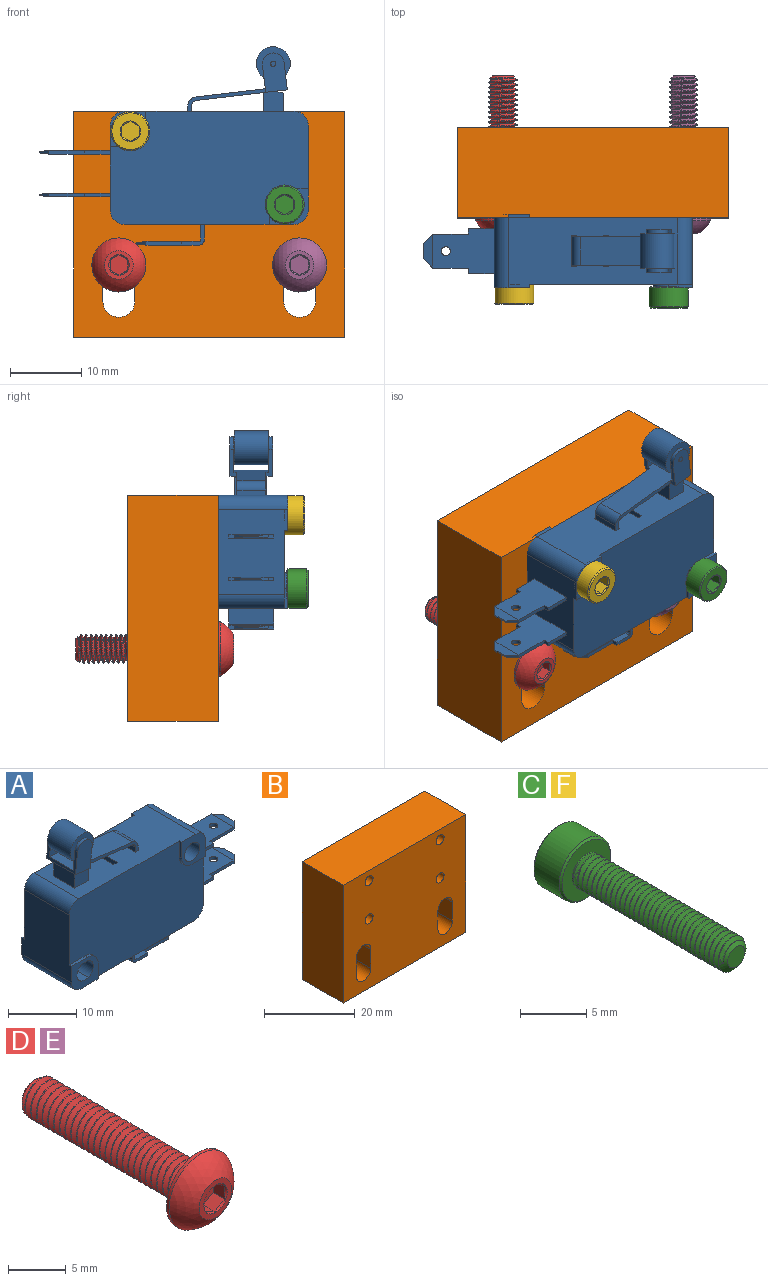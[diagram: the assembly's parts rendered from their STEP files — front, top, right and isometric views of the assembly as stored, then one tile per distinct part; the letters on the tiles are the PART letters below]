
ASSEMBLY  parts=6 mates=5
PART A: 124 faces, bbox 37.8x10.3x27.9 mm
  f0: cylinder r=0.64mm len=1.27mm, axis (0,0,1), area 2mm2, adj f84,f85
  f1: cylinder r=0.64mm len=1.27mm, axis (0,0,1), area 2mm2, adj f73,f74
  f2: cylinder r=0.64mm len=1.27mm, axis (0,0,1), area 2mm2, adj f51,f53
  f3: cylinder r=1.7mm len=10.31mm, axis (0,1,0), area 40.2mm2, adj f6,f11,f13,f15
  f4: cylinder r=1.55mm len=10.31mm, axis (0,1,0), area 100.4mm2, adj f5,f12
  f5: plane 5x5mm, normal (0,1,0), area 15.6mm2, adj f4,f9,f10,f19,f42,f43,f44
  f6: plane 5.5x5mm, normal (0,1,0), area 16.8mm2, adj f3,f7,f8,f13,f14,f15,f16,f45
  f7: plane 11.9x10.31mm, normal (-1,0,0), area 113.8mm2, adj f6,f11,f16,f18,f37,f41,f45,f48
  f8: plane 23.8x10.31mm, normal (0,0,-1), area 221.9mm2, adj f6,f11,f16,f17,f35,f41,f47,f48
  f9: plane 11.9x10.31mm, normal (1,0,0), area 107.3mm2, adj f5,f12,f17,f19,f40,f41,f42,f48
  f10: plane 23.8x10.31mm, normal (0,0,1), area 205.5mm2, adj f5,f12,f18,f19,f20,f21,f22,f23
  f11: plane 5.5x5mm, normal (0,-1,0), area 16.8mm2, adj f3,f7,f8,f13,f14,f15,f16,f35
  f12: plane 5x5mm, normal (0,-1,0), area 15.6mm2, adj f4,f9,f10,f19,f38,f39,f40
  f13: plane 10.31x1.4mm, normal (0,0,1), area 14.4mm2, adj f3,f6,f11,f14
  f14: cylinder r=1.7mm len=10.31mm, axis (0,1,0), area 40.2mm2, adj f6,f11,f13,f15
  f15: plane 10.31x1.4mm, normal (0,0,-1), area 14.4mm2, adj f3,f6,f11,f14
  f16: cylinder r=2mm len=10.31mm, axis (0,1,0), area 32.4mm2, adj f6,f7,f8,f11
  f17: cylinder r=2mm len=9.31mm, axis (0,1,0), area 29.2mm2, adj f8,f9,f41,f48
  f18: cylinder r=2mm len=9.31mm, axis (0,1,0), area 29.2mm2, adj f7,f10,f41,f48
  f19: cylinder r=2mm len=10.31mm, axis (0,1,0), area 32.4mm2, adj f5,f9,f10,f12
  f20: plane 2.85x2mm, normal (0,1,0), area 4.4mm2, adj f10,f21,f23,f24,f115,f116,f117
  f21: plane 4.25x2mm, normal (1,0,0), area 8.5mm2, adj f10,f20,f22,f24
  f22: plane 2.85x2mm, normal (0,-1,0), area 5.7mm2, adj f10,f21,f23,f24
  f23: plane 4.25x2mm, normal (-1,0,0), area 8.5mm2, adj f10,f20,f22,f24
  f24: plane 4.25x2.85mm, normal (0,0,1), area 12.1mm2, adj f20,f21,f22,f23
  f25: plane 4.25x2mm, normal (1,0,0), area 8.5mm2, adj f10,f26,f28,f29
  f26: plane 2x0.76mm, normal (0,-1,0), area 1.5mm2, adj f10,f25,f27,f29
  f27: plane 4.25x2mm, normal (-1,0,0), area 8.5mm2, adj f10,f26,f28,f29
  f28: plane 2x0.76mm, normal (0,1,0), area 1.5mm2, adj f10,f25,f27,f29
  f29: plane 4.25x0.76mm, normal (0,0,1), area 3.2mm2, adj f25,f26,f27,f28
  f30: plane 4.25x2mm, normal (1,0,0), area 8.5mm2, adj f10,f31,f33,f34
  f31: plane 2x0.76mm, normal (0,-1,0), area 1.5mm2, adj f10,f30,f32,f34
  f32: plane 4.25x2mm, normal (-1,0,0), area 8.5mm2, adj f10,f31,f33,f34
  f33: plane 2x0.76mm, normal (0,1,0), area 1.5mm2, adj f10,f30,f32,f34
  f34: plane 4.25x0.76mm, normal (0,0,1), area 3.2mm2, adj f30,f31,f32,f33
  f35: plane 2.8x0.5mm, normal (1,0,0), area 1.4mm2, adj f8,f11,f36,f41
  f36: cylinder r=2.2mm len=2.2mm, axis (0,-1,0), area 1.7mm2, adj f11,f35,f37,f41
  f37: plane 3.3x0.5mm, normal (0,0,1), area 1.6mm2, adj f7,f11,f36,f41
  f38: plane 2.8x0.5mm, normal (-1,0,0), area 1.4mm2, adj f10,f12,f39,f41
  f39: cylinder r=2.2mm len=2.2mm, axis (0,-1,0), area 1.7mm2, adj f12,f38,f40,f41
  f40: plane 2.8x0.5mm, normal (0,0,-1), area 1.4mm2, adj f9,f12,f39,f41
  f41: plane 27.8x15.9mm, normal (0,-1,0), area 389.9mm2, adj f7,f8,f9,f10,f17,f18,f35,f36
  f42: plane 2.8x0.5mm, normal (0,0,-1), area 1.4mm2, adj f5,f9,f43,f48
  f43: cylinder r=2.2mm len=2.2mm, axis (0,1,0), area 1.7mm2, adj f5,f42,f44,f48
  f44: plane 2.8x0.5mm, normal (-1,0,0), area 1.4mm2, adj f5,f10,f43,f48
  f45: plane 3.3x0.5mm, normal (0,0,1), area 1.6mm2, adj f6,f7,f46,f48
  f46: cylinder r=2.2mm len=2.2mm, axis (0,1,0), area 1.7mm2, adj f6,f45,f47,f48
  f47: plane 2.8x0.5mm, normal (1,0,0), area 1.4mm2, adj f6,f8,f46,f48
  f48: plane 27.8x15.9mm, normal (0,1,0), area 389.9mm2, adj f7,f8,f9,f10,f17,f18,f42,f43
  f49: plane 6.35x2.19mm, normal (-1,0,0), area 13.9mm2, adj f8,f50,f56,f57
  f50: cylinder r=0.71mm len=6.35mm, axis (0,1,0), area 7.1mm2, adj f49,f51,f56,f57
  f51: plane 7.48x6.35mm, normal (0,0,-1), area 38.1mm2, adj f2,f50,f56,f57,f59,f60,f61,f63
  f52: plane 2.12x0.17mm, normal (1,0,0), area 0.4mm2, adj f58,f62,f86,f87
  f53: plane 7.48x6.35mm, normal (0,0,1), area 38.1mm2, adj f2,f54,f56,f57,f59,f60,f61,f63
  f54: cylinder r=0.2mm len=6.35mm, axis (0,1,0), area 2mm2, adj f53,f55,f56,f57
  f55: plane 6.35x2.19mm, normal (1,0,0), area 13.9mm2, adj f8,f54,f56,f57
  f56: plane 3.15x2.9mm, normal (0,-1,0), area 2.7mm2, adj f8,f49,f50,f51,f53,f54,f55,f63
  f57: plane 3.15x2.9mm, normal (0,1,0), area 2.7mm2, adj f8,f49,f50,f51,f53,f54,f55,f60
  f58: plane 1.32x1.32mm, normal (0.71,0.71,0), area 0.6mm2, adj f52,f59,f86,f87
  f59: plane 5.03x0.51mm, normal (0,1,0), area 2.6mm2, adj f51,f53,f58,f60
  f60: plane 0.8x0.51mm, normal (1,0,0), area 0.4mm2, adj f51,f53,f57,f59
  f61: plane 5.03x0.51mm, normal (0,-1,0), area 2.6mm2, adj f51,f53,f62,f63
  f62: plane 1.32x1.32mm, normal (0.71,-0.71,0), area 0.6mm2, adj f52,f61,f86,f87
  f63: plane 0.8x0.51mm, normal (1,0,0), area 0.4mm2, adj f51,f53,f56,f61
  f64: plane 3.65x0.51mm, normal (0,1,0), area 1.9mm2, adj f9,f65,f73,f74
  f65: plane 0.8x0.51mm, normal (1,0,0), area 0.4mm2, adj f64,f66,f73,f74
  f66: plane 5.03x0.51mm, normal (0,1,0), area 2.6mm2, adj f65,f67,f73,f74
  f67: plane 1.32x1.32mm, normal (0.71,0.71,0), area 0.6mm2, adj f66,f68,f88,f89
  f68: plane 2.12x0.17mm, normal (1,0,0), area 0.4mm2, adj f67,f69,f88,f89
  f69: plane 1.32x1.32mm, normal (0.71,-0.71,0), area 0.6mm2, adj f68,f70,f88,f89
  f70: plane 5.03x0.51mm, normal (0,-1,0), area 2.6mm2, adj f69,f71,f73,f74
  f71: plane 0.8x0.51mm, normal (1,0,0), area 0.4mm2, adj f70,f72,f73,f74
  f72: plane 3.65x0.51mm, normal (0,-1,0), area 1.9mm2, adj f9,f71,f73,f74
  f73: plane 8.68x6.35mm, normal (0,0,-1), area 45.8mm2, adj f1,f9,f64,f65,f66,f70,f71,f72
  f74: plane 8.68x6.35mm, normal (0,0,1), area 45.8mm2, adj f1,f9,f64,f65,f66,f70,f71,f72
  f75: plane 3.65x0.51mm, normal (0,1,0), area 1.9mm2, adj f9,f76,f84,f85
  f76: plane 0.8x0.51mm, normal (1,0,0), area 0.4mm2, adj f75,f77,f84,f85
  f77: plane 5.03x0.51mm, normal (0,1,0), area 2.6mm2, adj f76,f78,f84,f85
  f78: plane 1.32x1.32mm, normal (0.71,0.71,0), area 0.6mm2, adj f77,f79,f90,f91
  f79: plane 2.12x0.17mm, normal (1,0,0), area 0.4mm2, adj f78,f80,f90,f91
  f80: plane 1.32x1.32mm, normal (0.71,-0.71,0), area 0.6mm2, adj f79,f81,f90,f91
  f81: plane 5.03x0.51mm, normal (0,-1,0), area 2.6mm2, adj f80,f82,f84,f85
  f82: plane 0.8x0.51mm, normal (1,0,0), area 0.4mm2, adj f81,f83,f84,f85
  f83: plane 3.65x0.51mm, normal (0,-1,0), area 1.9mm2, adj f9,f82,f84,f85
  f84: plane 8.68x6.35mm, normal (0,0,-1), area 45.8mm2, adj f0,f9,f75,f76,f77,f81,f82,f83
  f85: plane 8.68x6.35mm, normal (0,0,1), area 45.8mm2, adj f0,f9,f75,f76,f77,f81,f82,f83
  f86: plane 4.75x1.32mm, normal (0.13,0,0.99), area 4.6mm2, adj f52,f53,f58,f62
  f87: plane 4.75x1.32mm, normal (0.13,0,-0.99), area 4.6mm2, adj f51,f52,f58,f62
  f88: plane 4.75x1.32mm, normal (0.13,0,0.99), area 4.6mm2, adj f67,f68,f69,f74
  f89: plane 4.75x1.32mm, normal (0.13,0,-0.99), area 4.6mm2, adj f67,f68,f69,f73
  f90: plane 4.75x1.32mm, normal (0.13,0,0.99), area 4.6mm2, adj f78,f79,f80,f85
  f91: plane 4.75x1.32mm, normal (0.13,0,-0.99), area 4.6mm2, adj f78,f79,f80,f84
  f92: plane 2.8x2.8mm, normal (0,-1,0), area 7.6mm2, adj f10,f93,f112,f113,f116,f117
  f93: plane 12.76x6mm, normal (-0.12,0,-0.99), area 53.8mm2, adj f92,f100,f101,f103,f104,f106,f108,f110
  f94: cylinder r=0.38mm len=0.76mm, axis (0,1,0), area 1.3mm2, adj f104,f107
  f95: cylinder r=1.52mm len=3.04mm, axis (0,-1,0), area 2.7mm2, adj f100,f103,f105,f106
  f96: plane 12.76x4.88mm, normal (0.12,0,0.99), area 54.7mm2, adj f99,f100,f105,f106,f107,f108,f110,f111
  f97: plane 4.06x0.51mm, normal (0,0,-1), area 2.1mm2, adj f98,f102,f110,f111
  f98: plane 4.06x1.21mm, normal (1,0,0), area 4.9mm2, adj f97,f99,f110,f111
  f99: cylinder r=1.3mm len=4.06mm, axis (0,1,0), area 7.7mm2, adj f96,f98,f110,f111
  f100: plane 6x3.83mm, normal (-0.99,0,0.12), area 6.8mm2, adj f93,f95,f96,f103,f104,f105,f107,f109
  f101: cylinder r=0.79mm len=4.06mm, axis (0,1,0), area 4.7mm2, adj f93,f102,f110,f111
  f102: plane 4.06x1.21mm, normal (-1,0,0), area 4.9mm2, adj f97,f101,f110,f111
  f103: plane 5.53x3.49mm, normal (0,-1,0), area 15.4mm2, adj f93,f95,f100,f106
  f104: plane 5.53x3.49mm, normal (0,1,0), area 15mm2, adj f93,f94,f100,f108,f109
  f105: plane 5.03x3.43mm, normal (0,1,0), area 12.9mm2, adj f95,f96,f100,f106,f123
  f106: plane 3.83x0.97mm, normal (0.99,0,-0.12), area 2.4mm2, adj f93,f95,f96,f103,f105,f111
  f107: plane 5.03x3.43mm, normal (0,-1,0), area 13.4mm2, adj f94,f96,f100,f108,f109
  f108: plane 3.83x0.97mm, normal (0.99,0,-0.12), area 2.4mm2, adj f93,f96,f104,f107,f109,f110
  f109: cylinder r=1.52mm len=3.04mm, axis (0,1,0), area 2.7mm2, adj f100,f104,f107,f108
  f110: plane 10.94x3.65mm, normal (0,1,0), area 6.4mm2, adj f93,f96,f97,f98,f99,f101,f102,f108
  f111: plane 10.94x3.65mm, normal (0,-1,0), area 6.4mm2, adj f93,f96,f97,f98,f99,f101,f102,f106
  f112: cylinder r=4mm len=4.4mm, axis (0,1,0), area 2.1mm2, adj f92,f93,f114,f116
  f113: cylinder r=4mm len=4.4mm, axis (0,1,0), area 6.2mm2, adj f92,f93,f114,f117
  f114: plane 3.25x2.8mm, normal (0,1,0), area 8.9mm2, adj f93,f112,f113,f115,f116,f117
  f115: plane 4.23x2.8mm, normal (0,0,-1), area 11.8mm2, adj f20,f114,f116,f117
  f116: plane 4.4x3mm, normal (1,0,0), area 13.1mm2, adj f10,f20,f92,f112,f114,f115
  f117: plane 4.4x3mm, normal (-1,0,0), area 13.1mm2, adj f10,f20,f92,f113,f114,f115
  f118: plane 0.71x0.71mm, normal (0,1,0), area 0.4mm2, adj f122
  f119: plane 4.8x4.8mm, normal (0,1,0), area 17.7mm2, adj f121,f122
  f120: plane 4.8x4.8mm, normal (0,-1,0), area 17.1mm2, adj f121,f123
  f121: cylinder r=2.4mm len=4.8mm, axis (0,1,0), area 72.4mm2, adj f119,f120
  f122: cylinder r=0.36mm len=0.71mm, axis (0,-1,0), area 1.3mm2, adj f118,f119
  f123: cylinder r=0.56mm len=1.12mm, axis (0,-1,0), area 0.1mm2, adj f105,f120
PART B: 18 faces, bbox 38.1x12.7x31.8 mm
  f0: plane 38.1x31.75mm, normal (0,-1,0), area 1112.5mm2, adj f2,f3,f4,f5,f6,f7,f8,f9
  f1: plane 38.1x31.75mm, normal (0,1,0), area 1112.5mm2, adj f2,f3,f4,f5,f6,f7,f8,f9
  f2: plane 31.75x12.7mm, normal (1,0,0), area 403.2mm2, adj f0,f1,f3,f5
  f3: plane 38.1x12.7mm, normal (0,0,1), area 483.9mm2, adj f0,f1,f2,f4
  f4: plane 31.75x12.7mm, normal (-1,0,0), area 403.2mm2, adj f0,f1,f3,f5
  f5: plane 38.1x12.7mm, normal (0,0,-1), area 483.9mm2, adj f0,f1,f2,f4
  f6: cylinder r=1.25mm len=12.7mm, axis (0,-1,0), area 99.7mm2, adj f0,f1
  f7: cylinder r=1.25mm len=12.7mm, axis (0,-1,0), area 99.7mm2, adj f0,f1
  f8: cylinder r=1.25mm len=12.7mm, axis (0,-1,0), area 99.7mm2, adj f0,f1
  f9: cylinder r=1.25mm len=12.7mm, axis (0,-1,0), area 99.7mm2, adj f0,f1
  f10: cylinder r=2.25mm len=12.7mm, axis (0,-1,0), area 89.8mm2, adj f0,f1,f11,f13
  f11: plane 12.7x5.08mm, normal (-1,0,0), area 64.5mm2, adj f0,f1,f10,f12
  f12: cylinder r=2.25mm len=12.7mm, axis (0,-1,0), area 89.8mm2, adj f0,f1,f11,f13
  f13: plane 12.7x5.08mm, normal (1,0,0), area 64.5mm2, adj f0,f1,f10,f12
  f14: cylinder r=2.25mm len=12.7mm, axis (0,-1,0), area 89.8mm2, adj f0,f1,f15,f17
  f15: plane 12.7x5.08mm, normal (-1,0,0), area 64.5mm2, adj f0,f1,f14,f16
  f16: cylinder r=2.25mm len=12.7mm, axis (0,-1,0), area 89.8mm2, adj f0,f1,f15,f17
  f17: plane 12.7x5.08mm, normal (1,0,0), area 64.5mm2, adj f0,f1,f14,f16
PART C: 57 faces, bbox 6x19.6x6 mm
  f0: cylinder r=1.5mm len=3mm, axis (0,-1,0), area 0.3mm2, adj f1,f32,f33,f35,f36
  f1: cylinder r=1.5mm len=3mm, axis (0,-1,0), area 0.6mm2, adj f0,f2,f32,f33
  f2: cylinder r=1.5mm len=3mm, axis (0,-1,0), area 0.6mm2, adj f1,f3,f32,f33
  f3: cylinder r=1.5mm len=3mm, axis (0,-1,0), area 0.6mm2, adj f2,f4,f32,f33
  f4: cylinder r=1.5mm len=3mm, axis (0,-1,0), area 0.6mm2, adj f3,f5,f32,f33
  f5: cylinder r=1.5mm len=3mm, axis (0,-1,0), area 0.6mm2, adj f4,f6,f32,f33
  f6: cylinder r=1.5mm len=3mm, axis (0,-1,0), area 0.6mm2, adj f5,f7,f32,f33
  f7: cylinder r=1.5mm len=3mm, axis (0,-1,0), area 0.6mm2, adj f6,f8,f32,f33
  f8: cylinder r=1.5mm len=3mm, axis (0,-1,0), area 0.6mm2, adj f7,f9,f32,f33
  f9: cylinder r=1.5mm len=3mm, axis (0,-1,0), area 0.6mm2, adj f8,f10,f32,f33
  f10: cylinder r=1.5mm len=3mm, axis (0,-1,0), area 0.6mm2, adj f9,f11,f32,f33
  f11: cylinder r=1.5mm len=3mm, axis (0,-1,0), area 0.6mm2, adj f10,f12,f32,f33
  f12: cylinder r=1.5mm len=3mm, axis (0,-1,0), area 0.6mm2, adj f11,f13,f32,f33
  f13: cylinder r=1.5mm len=3mm, axis (0,-1,0), area 0.6mm2, adj f12,f14,f32,f33
  f14: cylinder r=1.5mm len=3mm, axis (0,-1,0), area 0.6mm2, adj f13,f15,f32,f33
  f15: cylinder r=1.5mm len=3mm, axis (0,-1,0), area 0.6mm2, adj f14,f16,f32,f33
  f16: cylinder r=1.5mm len=3mm, axis (0,-1,0), area 0.6mm2, adj f15,f17,f32,f33
  f17: cylinder r=1.5mm len=3mm, axis (0,-1,0), area 0.6mm2, adj f16,f18,f32,f33
  f18: cylinder r=1.5mm len=3mm, axis (0,-1,0), area 0.6mm2, adj f17,f19,f32,f33
  f19: cylinder r=1.5mm len=3mm, axis (0,-1,0), area 0.6mm2, adj f18,f20,f32,f33
  f20: cylinder r=1.5mm len=3mm, axis (0,-1,0), area 0.6mm2, adj f19,f21,f32,f33
  f21: cylinder r=1.5mm len=3mm, axis (0,-1,0), area 0.6mm2, adj f20,f22,f32,f33
  f22: cylinder r=1.5mm len=3mm, axis (0,-1,0), area 0.6mm2, adj f21,f23,f32,f33
  f23: cylinder r=1.5mm len=3mm, axis (0,-1,0), area 0.6mm2, adj f22,f24,f32,f33
  f24: cylinder r=1.5mm len=3mm, axis (0,-1,0), area 0.6mm2, adj f23,f25,f32,f33
  f25: cylinder r=1.5mm len=3mm, axis (0,-1,0), area 0.6mm2, adj f24,f26,f32,f33
  f26: cylinder r=1.5mm len=3mm, axis (0,-1,0), area 0.6mm2, adj f25,f27,f32,f33
  f27: cylinder r=1.5mm len=3mm, axis (0,-1,0), area 0.6mm2, adj f26,f28,f32,f33
  f28: cylinder r=1.5mm len=3mm, axis (0,-1,0), area 0.6mm2, adj f27,f29,f32,f33
  f29: cylinder r=1.5mm len=3mm, axis (0,-1,0), area 0.6mm2, adj f28,f30,f32,f33
  f30: cylinder r=1.5mm len=3mm, axis (0,-1,0), area 0.6mm2, adj f29,f31,f32,f33
  f31: cylinder r=1.5mm len=3mm, axis (0,-1,0), area 1.4mm2, adj f30,f32,f33,f40,f56
  f32: bspline ~16.1x3.46mm, area 97.9mm2, adj f0,f1,f2,f3,f4,f5,f6,f7
  f33: bspline ~15.85x3.46mm, area 97.9mm2, adj f0,f1,f2,f3,f4,f5,f6,f7
  f34: cylinder r=1.18mm len=15.56mm, axis (0,1,0), area 26.7mm2, adj f32,f33,f35,f56
  f35: cone r=0.92mm half-angle=55deg, axis (0,1,0), area 3.5mm2, adj f0,f32,f34,f36,f37
  f36: cone r=0.92mm half-angle=55deg, axis (0,1,0), area 0.1mm2, adj f0,f33,f35
  f37: plane 1.84x1.84mm, normal (0,-1,0), area 2.7mm2, adj f35
  f38: cylinder r=2.75mm len=5.5mm, axis (0,-1,0), area 46.1mm2, adj f54,f55
  f39: plane 5.17x5.17mm, normal (0,1,0), area 14.4mm2, adj f41,f42,f43,f44,f45,f46,f54
  f40: plane 5.17x5.17mm, normal (0,-1,0), area 13.9mm2, adj f31,f55
  f41: cone r=1.44mm half-angle=45deg, axis (0,1,0), area 0mm2, adj f39,f48
  f42: cone r=1.44mm half-angle=45deg, axis (0,1,0), area 0mm2, adj f39,f49
  f43: cone r=1.44mm half-angle=45deg, axis (0,1,0), area 0mm2, adj f39,f50
  f44: cone r=1.44mm half-angle=45deg, axis (0,1,0), area 0mm2, adj f39,f51
  f45: cone r=1.44mm half-angle=45deg, axis (0,1,0), area 0mm2, adj f39,f52
  f46: cone r=1.44mm half-angle=45deg, axis (0,1,0), area 0mm2, adj f39,f53
  f47: plane 2.89x2.5mm, normal (0,1,0), area 5.4mm2, adj f48,f49,f50,f51,f52,f53
  f48: plane 2.42x1.8mm, normal (-0.5,0,-0.87), area 2.5mm2, adj f41,f47,f49,f53
  f49: plane 2.42x1.99mm, normal (-1,0,0), area 2.5mm2, adj f42,f47,f48,f50
  f50: plane 2.42x1.8mm, normal (-0.5,0,0.87), area 2.5mm2, adj f43,f47,f49,f51
  f51: plane 2.42x1.8mm, normal (0.5,0,0.87), area 2.5mm2, adj f44,f47,f50,f52
  f52: plane 2.42x1.99mm, normal (1,0,0), area 2.5mm2, adj f45,f47,f51,f53
  f53: plane 2.42x1.8mm, normal (0.5,0,-0.87), area 2.5mm2, adj f46,f47,f48,f52
  f54: cone r=2.58mm half-angle=45deg, axis (0,-1,0), area 3.9mm2, adj f38,f39
  f55: cone r=2.75mm half-angle=45deg, axis (0,1,0), area 3.9mm2, adj f38,f40
  f56: cone r=1.5mm half-angle=67.5deg, axis (0,1,0), area 1.5mm2, adj f31,f32,f33,f34
PART D: 23 faces, bbox 8.2x23.4x8.2 mm
  f0: cone r=1.44mm half-angle=45deg, axis (0,-1,0), area 0.2mm2, adj f9,f17
  f1: cylinder r=3.8mm len=7.6mm, axis (0,-1,0), area 7.9mm2, adj f2,f10
  f2: sphere r=4.23mm, area 49.8mm2, adj f1,f9
  f3: cone r=1.47mm half-angle=45deg, axis (0,-1,0), area 4.4mm2, adj f4,f5,f6,f7,f8
  f4: cylinder r=2mm len=19.48mm, axis (0,1,0), area 30.6mm2, adj f3,f6,f8,f10
  f5: plane 2.95x2.95mm, normal (0,1,0), area 6.8mm2, adj f3
  f6: bspline ~20.33x4.62mm, area 164.8mm2, adj f3,f4,f7,f10
  f7: bspline ~20.27x3.57mm, area 24.1mm2, adj f3,f6,f8,f10
  f8: bspline ~20.45x3.99mm, area 164.7mm2, adj f3,f4,f7,f10
  f9: plane 4.47x4.47mm, normal (0,-1,0), area 6mm2, adj f0,f2,f11,f12,f13,f14,f15
  f10: plane 7.87x7.87mm, normal (0,1,0), area 35.4mm2, adj f1,f4,f6,f7,f8
  f11: cone r=1.44mm half-angle=45deg, axis (0,-1,0), area 0mm2, adj f9,f18
  f12: cone r=1.44mm half-angle=45deg, axis (0,-1,0), area 0mm2, adj f9,f19
  f13: cone r=1.44mm half-angle=45deg, axis (0,-1,0), area 0mm2, adj f9,f20
  f14: cone r=1.44mm half-angle=45deg, axis (0,-1,0), area 0mm2, adj f9,f21
  f15: cone r=1.44mm half-angle=45deg, axis (0,-1,0), area 0mm2, adj f9,f22
  f16: plane 2.89x2.5mm, normal (0,-1,0), area 5.4mm2, adj f17,f18,f19,f20,f21,f22
  f17: plane 1.68x1.58mm, normal (-1,0,0), area 2mm2, adj f0,f16,f18,f22
  f18: plane 2.09x1.8mm, normal (-0.5,0,-0.87), area 2mm2, adj f11,f16,f17,f19
  f19: plane 2.09x1.8mm, normal (0.5,0,-0.87), area 2mm2, adj f12,f16,f18,f20
  f20: plane 2.09x1.99mm, normal (1,0,0), area 2mm2, adj f13,f16,f19,f21
  f21: plane 2.09x1.8mm, normal (0.5,0,0.87), area 2mm2, adj f14,f16,f20,f22
  f22: plane 2.09x1.8mm, normal (-0.5,0,0.87), area 2mm2, adj f15,f16,f17,f21
PART E: same geometry as D
PART F: same geometry as C
PLACE A rot(axis=(0,0,1),180deg) t=(19.05,-17.36,23.81)mm
PLACE B rot(axis=(0,0,1),180deg) t=(19.05,-6.35,15.88)mm
PLACE C rot(axis=(0,0,1),180deg) t=(29.65,-6.35,18.66)mm
PLACE D t=(6.35,-14.9,10.16)mm
PLACE E t=(31.75,-14.9,10.16)mm
PLACE F rot(axis=(0,0,1),180deg) t=(7.95,-5.85,28.96)mm
MATE fastened A.f4 <-> B.f7  axis (0,1,0) through (7.95,-12.7,28.96)mm
MATE fastened E.f0 <-> B.f12  axis (0,1,0) through (31.75,-12.7,10.16)mm
MATE fastened A.f36 <-> C.f0  axis (0,-1,0) through (29.65,-22.51,18.66)mm
MATE fastened A.f4 <-> F.f0  axis (0,-1,0) through (7.95,-22.01,28.96)mm
MATE fastened B.f16 <-> D.f0  axis (0,-1,0) through (6.35,-12.7,10.16)mm
